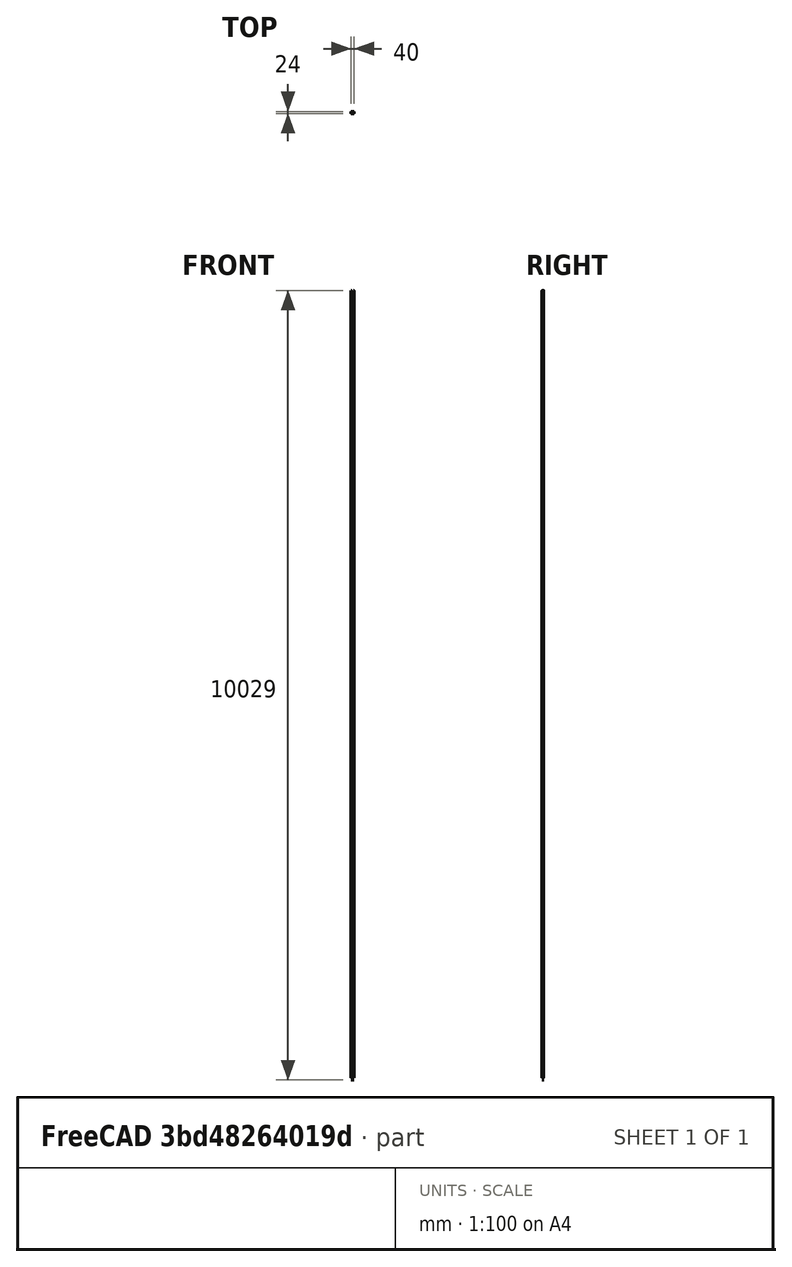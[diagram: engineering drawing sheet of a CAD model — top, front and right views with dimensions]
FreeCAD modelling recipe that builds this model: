
FCSTD DOCUMENT  (FreeCAD 0.15R4671 (Git))
Label: lm8uu-mount-spacer
License: All rights reserved
LicenseURL: http://en.wikipedia.org/wiki/All_rights_reserved
objects: Mesh::Feature×1, Part::Box×1, Sketcher::SketchObject×1, PartDesign::Pocket×1
note: 4 computed .brp shape members not serialized (recipe doc carries the construction recipe); baked Part::Feature solids carry a one-line shape summary decoded from their .brp

FEATURE [Mesh::Feature] lm8uu_round_split_xnaron  label="lm8uu-round-split-xnaron"
  Placement = pos=(0,0,0) rot=(-1,0,0;1.5708rad)
FEATURE [Part::Box] Box  label="Cube"
  Height = 5
  Length = 40
  Placement = pos=(1,0,-29) rot=(0,0,1;0rad)
  Width = 24
FEATURE [Sketcher::SketchObject] Sketch
  Placement = pos=(1,0,-29) rot=(1,0,0;3.14159rad)
  Support = -> Box [Face5]
  sketch-geometry (4):
    g0: Circle CenterX=4.5 CenterY=-5 CenterZ=0 NormalX=0 NormalY=0 NormalZ=1 Radius=2.5
    g1: Circle CenterX=4.5 CenterY=-19 CenterZ=0 NormalX=0 NormalY=0 NormalZ=1 Radius=2.5
    g2: Circle CenterX=35.5 CenterY=-5 CenterZ=0 NormalX=0 NormalY=0 NormalZ=1 Radius=2.5
    g3: Circle CenterX=35.5 CenterY=-19 CenterZ=0 NormalX=0 NormalY=0 NormalZ=1 Radius=2.5
  constraints (12):
    c: Radius(g0) = 2.5
    c: Equal(g0,g1)
    c: Equal(g1,g2)
    c: Equal(g2,g3)
    c: DistanceY(g0,g1) = -14
    c: DistanceX(g0,g1) = 0
    c: DistanceY(g0,g2) = 0
    c: DistanceX(g3,g2) = 0
    c: DistanceY(g3,g1) = 0
    c: DistanceY(g-1,g0) = -5
    c: DistanceX(g-1,g0) = 4.5
    c: DistanceX(g0,g2) = 31
FEATURE [PartDesign::Pocket] Pocket
  Length = 5
  Placement = pos=(1,0,-29) rot=(0,0,1;0rad)
  Sketch = -> Sketch
  Type = 1
